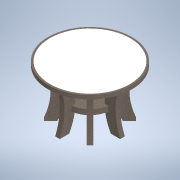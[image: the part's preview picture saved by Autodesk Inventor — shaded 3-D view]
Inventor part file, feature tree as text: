
AUTODESK INVENTOR PART (.ipt)
format: ipt  version: 2022 (Build 260153000, 153)  size: 233,984 bytes
history: native  units: mm
features: extrude x4, sketch x4, direct_edit x2, other x2, shell x1, pattern_circular x1, plane x1
ambient origin geometry x8: Origin, YZ Plane, XZ Plane, XY Plane, X Axis, Y Axis, Z Axis, Center Point
bodies: Solid1 (feature_tree), Solid2 (feature_tree), Solid3 (feature_tree), Solid4 (feature_tree)
feature tree (15):
  extrude  "Extrusion1"  Depth=2.0mm TaperAngle=0.0deg
  shell  "Shell1"  Thickness=1.0mm
  extrude  "Extrusion2"  Depth=1.0mm TaperAngle=0.0deg
  extrude  "Extrusion3"  Depth=25.0mm
  pattern_circular  "Circular Pattern1"  [2 undecoded]
  plane  "Work Plane1"
  extrude  "Extrusion4"  Depth=10.0mm
  direct_edit  "Direct Edit1"
  direct_edit  "Direct Edit2"
  sketch  "Sketch1"  dims[d0=45.0mm d1=2.0mm d2=0.0mm d3=1.0mm]
  sketch  "Sketch2"  dims[d4=43.0mm d5=1.0mm d6=0.0mm]
  sketch  "Sketch3"  dims[d7=5.0mm d8=25.0mm]
  sketch  "Sketch4"  dims[d9=25.0mm d10=5.0mm d11=5.0mm d12=2.5mm d13=0.0mm d14=80.0mm d15=360.0deg d17=12.5mm d18=20.0mm d19=2.5mm d20=0.0mm d21=7.5mm d22=10.0mm d23=10.0mm d24=9.0mm d25=10.0mm d26=10.0mm]
  other  "Scale1"
  other  "Scale2"
note: 2 required parameter values undecoded (feature->parameter linkage not recoverable at this tier; creation-order binding heuristic only, values carry confidence <= 0.55)
